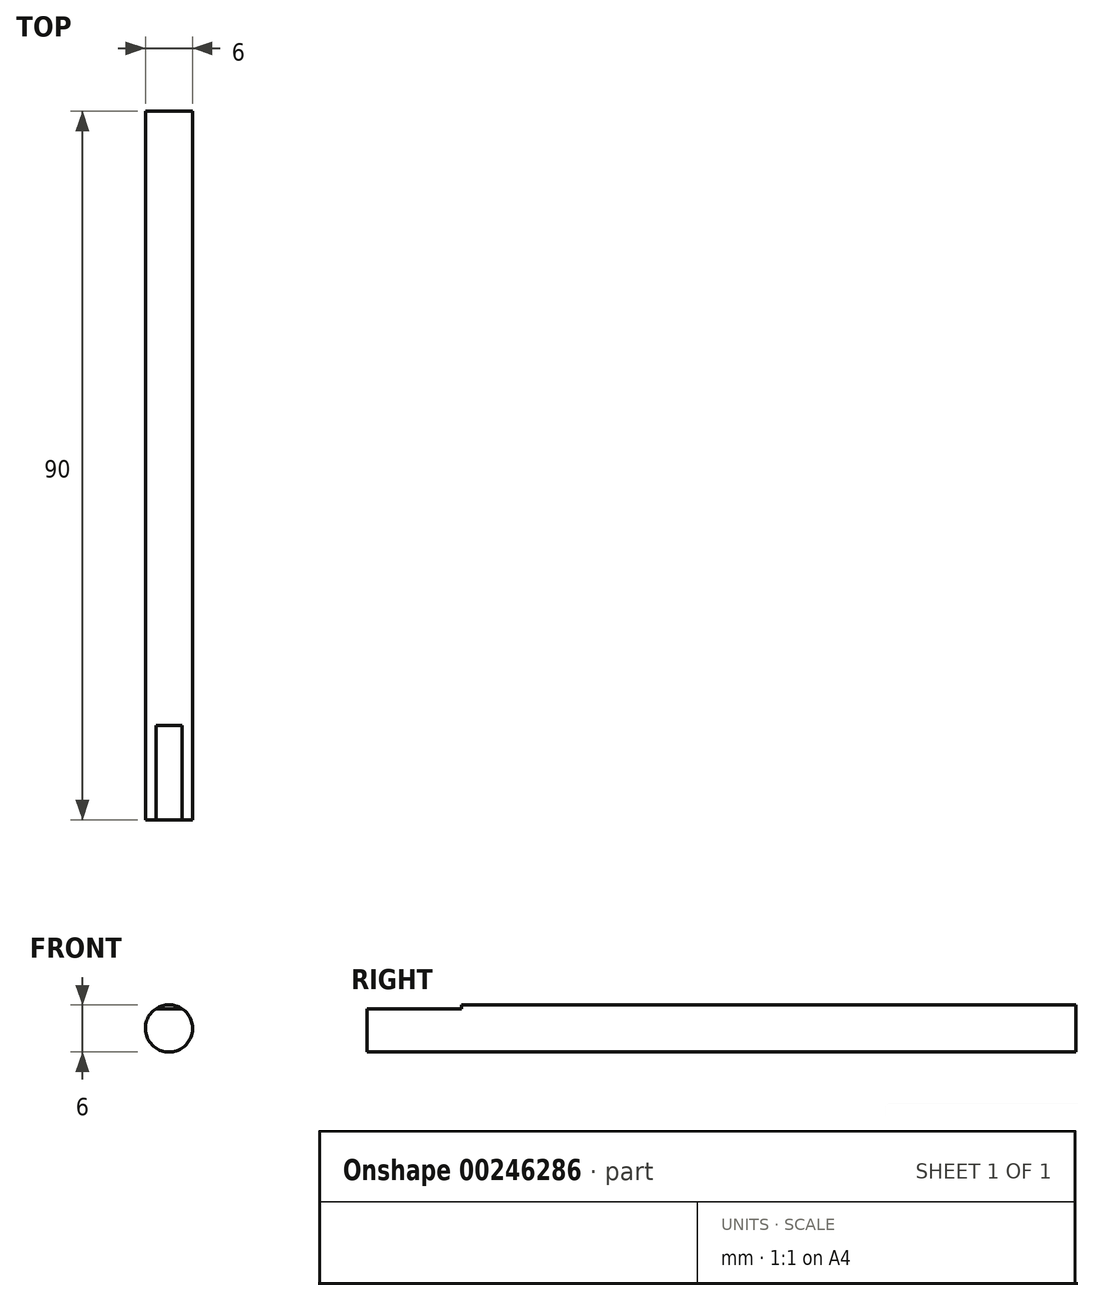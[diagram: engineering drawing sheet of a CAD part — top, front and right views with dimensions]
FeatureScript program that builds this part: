
annotation { "Feature Type Name" : "Feature", "Feature Type Description" : "" }
export const myFeature = defineFeature(function(context is Context, id is Id, definition is map)
    precondition{}
    {
        {
            var Q0;
            Q0=qCreatedBy(makeId("Front.planeOp"),FACE);
            var sketch = newSketch(context, id + "F0", { "sketchPlane" : qUnion([Q0])});
            skCircle(sketch, "E0", {"center": v(0, 0) * mm, "radius": 3 * mm});
            skSolve(sketch);
        }
        {
            var Q0;
            Q0 = qSketchRegion(id + "F0", true);
            extrude(context, id + "F1", {"entities" : qUnion([Q0]), "depth" : 90 * mm});
        }
        {
            var Q0;
            Q0=makeQuery(id+"F1.opExtrude","CAP_FACE",FACE,{"disambiguationData":[OSD([sQuery(id+"F0.wireOp",EDGE,"E0")])],"isStart":false});
            var sketch = newSketch(context, id + "F2", { "sketchPlane" : qUnion([Q0])});
            skLineSegment(sketch, "E1.bottom", {"start": v(-3.04, 4.85) * mm, "end": v(4.67, 4.85) * mm});
            skLineSegment(sketch, "E1.top", {"start": v(-3.04, 2.5) * mm, "end": v(4.67, 2.5) * mm});
            skLineSegment(sketch, "E1.left", {"start": v(-3.04, 4.85) * mm, "end": v(-3.04, 2.5) * mm});
            skLineSegment(sketch, "E1.right", {"start": v(4.67, 4.85) * mm, "end": v(4.67, 2.5) * mm});
            skSolve(sketch);
        }
        {
            var Q0;
            Q0 = qSketchRegion(id + "F2", true);
            extrude(context, id + "F3", {"entities" : qUnion([Q0]), "operationType" : NewBodyOperationType.REMOVE, "oppositeDirection" : true, "depth" : 12 * mm});
        }
    });
